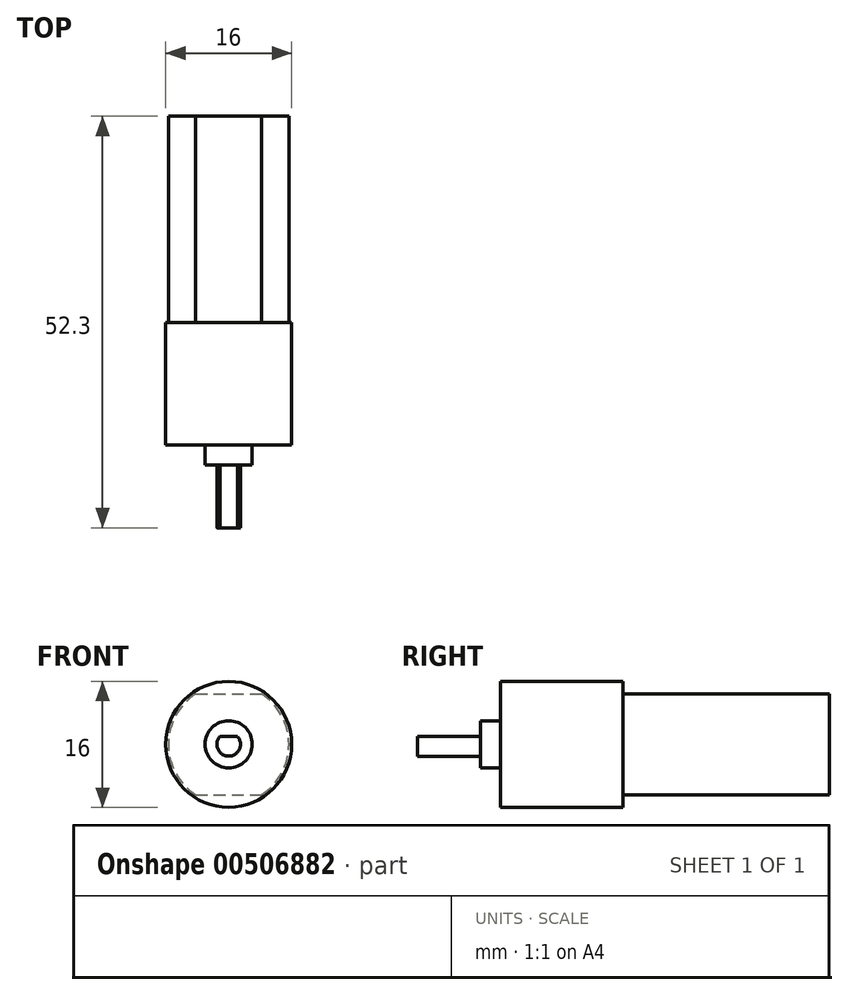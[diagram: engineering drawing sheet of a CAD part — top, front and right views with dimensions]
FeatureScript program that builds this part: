
annotation { "Feature Type Name" : "Feature", "Feature Type Description" : "" }
export const myFeature = defineFeature(function(context is Context, id is Id, definition is map)
    precondition{}
    {
        {
            var Q0;
            Q0=qCreatedBy(makeId("Front.planeOp"),FACE);
            var sketch = newSketch(context, id + "F0", { "sketchPlane" : qUnion([Q0])});
            skArc(sketch, "E0", {"start": v(-4.2, 6.4) * mm, "mid": v(-7.65, 0) * mm, "end": v(-4.2, -6.4) * mm});
            skLineSegment(sketch, "E1", {"start": v(0, 0) * mm, "end": v(7.65, 0) * mm, "construction": true});
            skLineSegment(sketch, "E2", {"start": v(-4.2, 6.4) * mm, "end": v(4.2, 6.4) * mm});
            skLineSegment(sketch, "E3.MirrorCS", {"start": v(-4.2, -6.4) * mm, "end": v(4.2, -6.4) * mm});
            skArc(sketch, "E4.trimOffspring", {"start": v(4.2, -6.4) * mm, "mid": v(7.65, 0) * mm, "end": v(4.2, 6.4) * mm});
            skSolve(sketch);
        }
        {
            var Q0;
            Q0 = qSketchRegion(id + "F0", true);
            extrude(context, id + "F1", {"entities" : qUnion([Q0]), "oppositeDirection" : true, "depth" : 26.2 * mm, "offsetDistance" : 25 * mm});
        }
        {
            var Q0;
            Q0=makeQuery(id+"F1.opExtrude","CAP_FACE",FACE,{"disambiguationData":[OSD([sQuery(id+"F0.wireOp",EDGE,"E0"),sQuery(id+"F0.wireOp",EDGE,"E2"),sQuery(id+"F0.wireOp",EDGE,"E3.MirrorCS"),sQuery(id+"F0.wireOp",EDGE,"E4.trimOffspring")])],"isStart":true});
            var sketch = newSketch(context, id + "F2", { "sketchPlane" : qUnion([Q0])});
            skCircle(sketch, "E5", {"center": v(0, 0) * mm, "radius": 8 * mm});
            skSolve(sketch);
        }
        {
            var Q0;
            Q0 = qSketchRegion(id + "F2", true);
            extrude(context, id + "F3", {"entities" : qUnion([Q0]), "operationType" : NewBodyOperationType.ADD, "depth" : 15.6 * mm, "offsetDistance" : 25 * mm});
        }
        {
            var Q0;
            Q0=makeQuery(id+"F3.opExtrude","CAP_FACE",FACE,{"disambiguationData":[OSD([sQuery(id+"F2.wireOp",EDGE,"E5")])],"isStart":false});
            var sketch = newSketch(context, id + "F4", { "sketchPlane" : qUnion([Q0])});
            skArc(sketch, "E6", {"start": v(-1.12, 1) * mm, "mid": v(0, -1.5) * mm, "end": v(1.12, 1) * mm});
            skLineSegment(sketch, "E7", {"start": v(-1.12, 1) * mm, "end": v(1.12, 1) * mm});
            skLineSegment(sketch, "E8", {"start": v(0, 1) * mm, "end": v(0, -1.5) * mm, "construction": true});
            skSolve(sketch);
        }
        {
            var Q0;
            Q0 = qSketchRegion(id + "F4", true);
            extrude(context, id + "F5", {"entities" : qUnion([Q0]), "operationType" : NewBodyOperationType.ADD, "depth" : 10.5 * mm, "offsetDistance" : 25 * mm});
        }
        {
            var Q0;
            Q0=makeQuery(id+"F3.opExtrude","CAP_FACE",FACE,{"disambiguationData":[OSD([sQuery(id+"F2.wireOp",EDGE,"E5")])],"isStart":false});
            var sketch = newSketch(context, id + "F6", { "sketchPlane" : qUnion([Q0])});
            skCircle(sketch, "E9", {"center": v(0, 0) * mm, "radius": 3 * mm});
            skSolve(sketch);
        }
        {
            var Q0;
            Q0 = qSketchRegion(id + "F6", true);
            extrude(context, id + "F7", {"entities" : qUnion([Q0]), "operationType" : NewBodyOperationType.ADD, "depth" : 2.5 * mm, "offsetDistance" : 25 * mm});
        }
        {
            var Q0;
            Q0=makeQuery(id+"F3.opExtrude","CAP_FACE",FACE,{"disambiguationData":[OSD([sQuery(id+"F2.wireOp",EDGE,"E5")])],"isStart":false});
            var sketch = newSketch(context, id + "F8", { "sketchPlane" : qUnion([Q0])});
            skCircle(sketch, "E10", {"center": v(-13.13, 0) * mm, "radius": 1.94 * mm});
            skLineSegment(sketch, "E11", {"start": v(0, 0) * mm, "end": v(0, 12.64) * mm, "construction": true});
            skCircle(sketch, "E12.MirrorC", {"center": v(13.13, 0) * mm, "radius": 1.94 * mm});
            skSolve(sketch);
        }
        {
            var Q0;
            Q0 = qSketchRegion(id + "F8", true);
            extrude(context, id + "F9", {"entities" : qUnion([Q0]), "operationType" : NewBodyOperationType.REMOVE, "oppositeDirection" : true, "depth" : 20 * mm});
        }
    });
